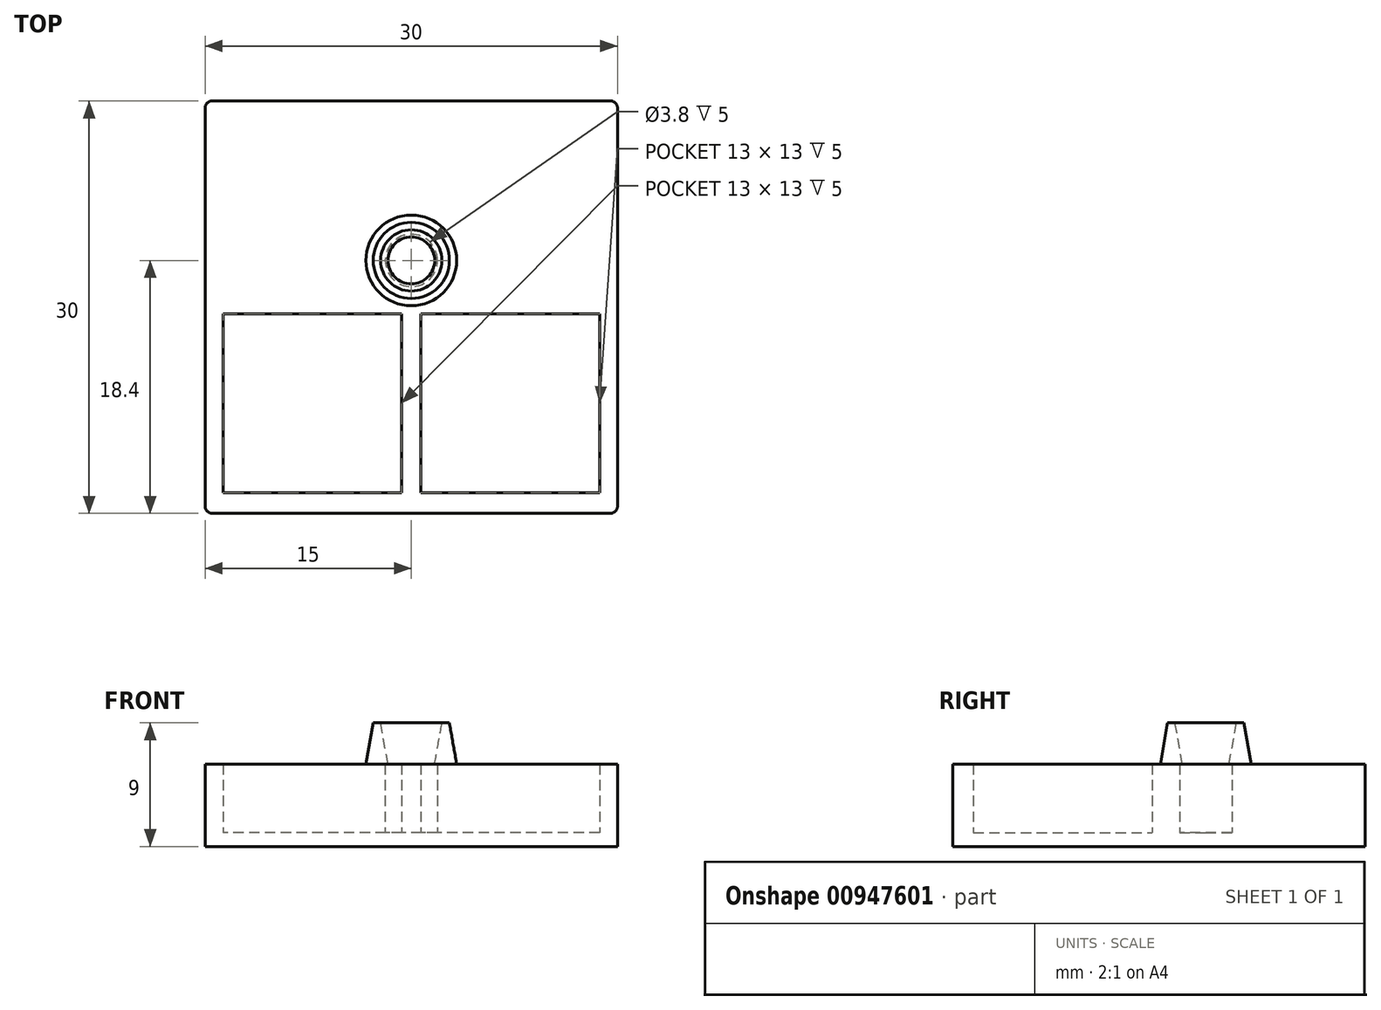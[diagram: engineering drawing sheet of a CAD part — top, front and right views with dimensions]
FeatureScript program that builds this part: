
annotation { "Feature Type Name" : "Feature", "Feature Type Description" : "" }
export const myFeature = defineFeature(function(context is Context, id is Id, definition is map)
    precondition{}
    {
        {
            var Q0;
            Q0=qCreatedBy(makeId("Top.planeOp"),FACE);
            var sketch = newSketch(context, id + "F0", { "sketchPlane" : qUnion([Q0])});
            skCircle(sketch, "E0", {"center": v(0, 3.4) * mm, "radius": 1.9 * mm});
            skLineSegment(sketch, "E1.bottom", {"start": v(-15, 15) * mm, "end": v(15, 15) * mm, "construction": true});
            skLineSegment(sketch, "E1.top", {"start": v(-15, -15) * mm, "end": v(15, -15) * mm, "construction": true});
            skLineSegment(sketch, "E1.left", {"start": v(-15, 15) * mm, "end": v(-15, -15) * mm, "construction": true});
            skLineSegment(sketch, "E1.right", {"start": v(15, 15) * mm, "end": v(15, -15) * mm, "construction": true});
            skPoint(sketch, "E1.middle", {"position": v(0, 0) * mm});
            skLineSegment(sketch, "E2.bottom", {"start": v(-0.7, -13.5) * mm, "end": v(-13.7, -13.5) * mm});
            skLineSegment(sketch, "E2.top", {"start": v(-0.7, -0.5) * mm, "end": v(-13.7, -0.5) * mm});
            skLineSegment(sketch, "E2.left", {"start": v(-0.7, -13.5) * mm, "end": v(-0.7, -0.5) * mm});
            skLineSegment(sketch, "E2.right", {"start": v(-13.7, -13.5) * mm, "end": v(-13.7, -0.5) * mm});
            skPoint(sketch, "E2.middle", {"position": v(-7.2, -7) * mm});
            skLineSegment(sketch, "E3.bottom", {"start": v(13.7, -13.5) * mm, "end": v(0.7, -13.5) * mm});
            skLineSegment(sketch, "E3.top", {"start": v(13.7, -0.5) * mm, "end": v(0.7, -0.5) * mm});
            skLineSegment(sketch, "E3.left", {"start": v(13.7, -13.5) * mm, "end": v(13.7, -0.5) * mm});
            skLineSegment(sketch, "E3.right", {"start": v(0.7, -13.5) * mm, "end": v(0.7, -0.5) * mm});
            skPoint(sketch, "E3.middle", {"position": v(7.2, -7) * mm});
            skLineSegment(sketch, "E4", {"start": v(-15, 15) * mm, "end": v(-15, -15) * mm});
            skLineSegment(sketch, "E5", {"start": v(-15, -15) * mm, "end": v(15, -15) * mm});
            skLineSegment(sketch, "E6", {"start": v(15, -15) * mm, "end": v(15, 15) * mm});
            skLineSegment(sketch, "E7", {"start": v(-15, 15) * mm, "end": v(15, 15) * mm});
            skSolve(sketch);
        }
        {
            var Q0;
            Q0 = qSketchRegion(id + "F0", true);
            extrude(context, id + "F1", {"entities" : qUnion([Q0]), "depth" : 5 * mm, "offsetDistance" : 25 * mm});
        }
        {
            var Q0;
            Q0=makeQuery(id+"F1.opExtrude","CAP_FACE",FACE,{"disambiguationData":[OSD([sQuery(id+"F0.wireOp",EDGE,"E0"),sQuery(id+"F0.wireOp",EDGE,"E2.bottom"),sQuery(id+"F0.wireOp",EDGE,"E2.top"),sQuery(id+"F0.wireOp",EDGE,"E2.left"),sQuery(id+"F0.wireOp",EDGE,"E2.right"),sQuery(id+"F0.wireOp",EDGE,"E3.bottom"),sQuery(id+"F0.wireOp",EDGE,"E3.top"),sQuery(id+"F0.wireOp",EDGE,"E3.left"),sQuery(id+"F0.wireOp",EDGE,"E3.right"),sQuery(id+"F0.wireOp",EDGE,"E4"),sQuery(id+"F0.wireOp",EDGE,"E5"),sQuery(id+"F0.wireOp",EDGE,"E6"),sQuery(id+"F0.wireOp",EDGE,"tpcU3x32-NjBL-OoPL-dwks-4QMxZsZ76EQ4.bottom"),sQuery(id+"F0.wireOp",EDGE,"tpcU3x32-NjBL-OoPL-dwks-4QMxZsZ76EQ4.top"),sQuery(id+"F0.wireOp",EDGE,"tpcU3x32-NjBL-OoPL-dwks-4QMxZsZ76EQ4.left"),sQuery(id+"F0.wireOp",EDGE,"tpcU3x32-NjBL-OoPL-dwks-4QMxZsZ76EQ4.right"),sQuery(id+"F0.wireOp",EDGE,"E7")])],"isStart":false});
            var sketch = newSketch(context, id + "F2", { "sketchPlane" : qUnion([Q0])});
            skCircle(sketch, "E8", {"center": v(0, 3.4) * mm, "radius": 3.3 * mm});
            skCircle(sketch, "E9", {"center": v(0, 3.4) * mm, "radius": 1.7 * mm});
            skSolve(sketch);
        }
        {
            var Q0;
            Q0 = qSketchRegion(id + "F2", true);
            extrude(context, id + "F3", {"entities" : qUnion([Q0]), "operationType" : NewBodyOperationType.ADD, "depth" : 3 * mm, "offsetDistance" : 25 * mm, "hasDraft" : true, "draftAngle" : 10 * degree, "draftPullDirection" : true});
        }
        {
            var Q0;
            Q0=makeQuery(id+"F1.opExtrude","CAP_FACE",FACE,{"disambiguationData":[OSD([sQuery(id+"F0.wireOp",EDGE,"E0"),sQuery(id+"F0.wireOp",EDGE,"E2.bottom"),sQuery(id+"F0.wireOp",EDGE,"E2.top"),sQuery(id+"F0.wireOp",EDGE,"E2.left"),sQuery(id+"F0.wireOp",EDGE,"E2.right"),sQuery(id+"F0.wireOp",EDGE,"E3.bottom"),sQuery(id+"F0.wireOp",EDGE,"E3.top"),sQuery(id+"F0.wireOp",EDGE,"E3.left"),sQuery(id+"F0.wireOp",EDGE,"E3.right"),sQuery(id+"F0.wireOp",EDGE,"E4"),sQuery(id+"F0.wireOp",EDGE,"E5"),sQuery(id+"F0.wireOp",EDGE,"E6"),sQuery(id+"F0.wireOp",EDGE,"tpcU3x32-NjBL-OoPL-dwks-4QMxZsZ76EQ4.bottom"),sQuery(id+"F0.wireOp",EDGE,"tpcU3x32-NjBL-OoPL-dwks-4QMxZsZ76EQ4.top"),sQuery(id+"F0.wireOp",EDGE,"tpcU3x32-NjBL-OoPL-dwks-4QMxZsZ76EQ4.left"),sQuery(id+"F0.wireOp",EDGE,"tpcU3x32-NjBL-OoPL-dwks-4QMxZsZ76EQ4.right"),sQuery(id+"F0.wireOp",EDGE,"E7")])],"isStart":true});
            var sketch = newSketch(context, id + "F4", { "sketchPlane" : qUnion([Q0])});
            skLineSegment(sketch, "E10.bottom", {"start": v(-15, 15) * mm, "end": v(15, 15) * mm});
            skLineSegment(sketch, "E10.top", {"start": v(-15, -15) * mm, "end": v(15, -15) * mm});
            skLineSegment(sketch, "E10.left", {"start": v(-15, 15) * mm, "end": v(-15, -15) * mm});
            skLineSegment(sketch, "E10.right", {"start": v(15, 15) * mm, "end": v(15, -15) * mm});
            skPoint(sketch, "E10.middle", {"position": v(0, 0) * mm});
            skSolve(sketch);
        }
        {
            var Q0;
            Q0 = qSketchRegion(id + "F4", true);
            extrude(context, id + "F5", {"entities" : qUnion([Q0]), "operationType" : NewBodyOperationType.ADD, "depth" : 1 * mm, "offsetDistance" : 25 * mm});
        }
        {
            var Q0;
            Q0=makeQuery(id+"F5.boolean.opBoolean","MERGE",EDGE,{"derivedFrom":[makeQuery(id+"F1.opExtrude","SWEPT_EDGE",EDGE,{"disambiguationData":[OSD([sQuery(id+"F0.wireOp",EDGE,"E4"),sQuery(id+"F0.wireOp",EDGE,"E5")])]}),makeQuery(id+"F5.opExtrude","SWEPT_EDGE",EDGE,{"disambiguationData":[OSD([sQuery(id+"F4.wireOp",EDGE,"E10.bottom"),sQuery(id+"F4.wireOp",EDGE,"E10.left")])]})]});
            var Q1;
            Q1=makeQuery(id+"F5.boolean.opBoolean","MERGE",EDGE,{"derivedFrom":[makeQuery(id+"F1.opExtrude","SWEPT_EDGE",EDGE,{"disambiguationData":[OSD([sQuery(id+"F0.wireOp",EDGE,"E5"),sQuery(id+"F0.wireOp",EDGE,"E6")])]}),makeQuery(id+"F5.opExtrude","SWEPT_EDGE",EDGE,{"disambiguationData":[OSD([sQuery(id+"F4.wireOp",EDGE,"E10.bottom"),sQuery(id+"F4.wireOp",EDGE,"E10.right")])]})]});
            var Q2;
            Q2=makeQuery(id+"F5.boolean.opBoolean","MERGE",EDGE,{"derivedFrom":[makeQuery(id+"F1.opExtrude","SWEPT_EDGE",EDGE,{"disambiguationData":[OSD([sQuery(id+"F0.wireOp",EDGE,"E6"),sQuery(id+"F0.wireOp",EDGE,"E7")])]}),makeQuery(id+"F5.opExtrude","SWEPT_EDGE",EDGE,{"disambiguationData":[OSD([sQuery(id+"F4.wireOp",EDGE,"E10.top"),sQuery(id+"F4.wireOp",EDGE,"E10.right")])]})]});
            var Q3;
            Q3=makeQuery(id+"F5.boolean.opBoolean","MERGE",EDGE,{"derivedFrom":[makeQuery(id+"F1.opExtrude","SWEPT_EDGE",EDGE,{"disambiguationData":[OSD([sQuery(id+"F0.wireOp",EDGE,"E4"),sQuery(id+"F0.wireOp",EDGE,"E7")])]}),makeQuery(id+"F5.opExtrude","SWEPT_EDGE",EDGE,{"disambiguationData":[OSD([sQuery(id+"F4.wireOp",EDGE,"E10.top"),sQuery(id+"F4.wireOp",EDGE,"E10.left")])]})]});
            var Q4;
            Q4=makeQuery(id+"F3.opExtrude","CAP_EDGE",EDGE,{"disambiguationData":[OSD([sQuery(id+"F2.wireOp",EDGE,"E8")])],"isStart":true});
            fillet(context, id + "F6", {"entities" : qUnion([Q0, Q1, Q2, Q3, Q4]), "tangentPropagation" : true, "radius" : .5 * mm, "defaultsChanged" : false, "vertexSettings" : [], "allowEdgeOverflow" : false});
        }
    });
